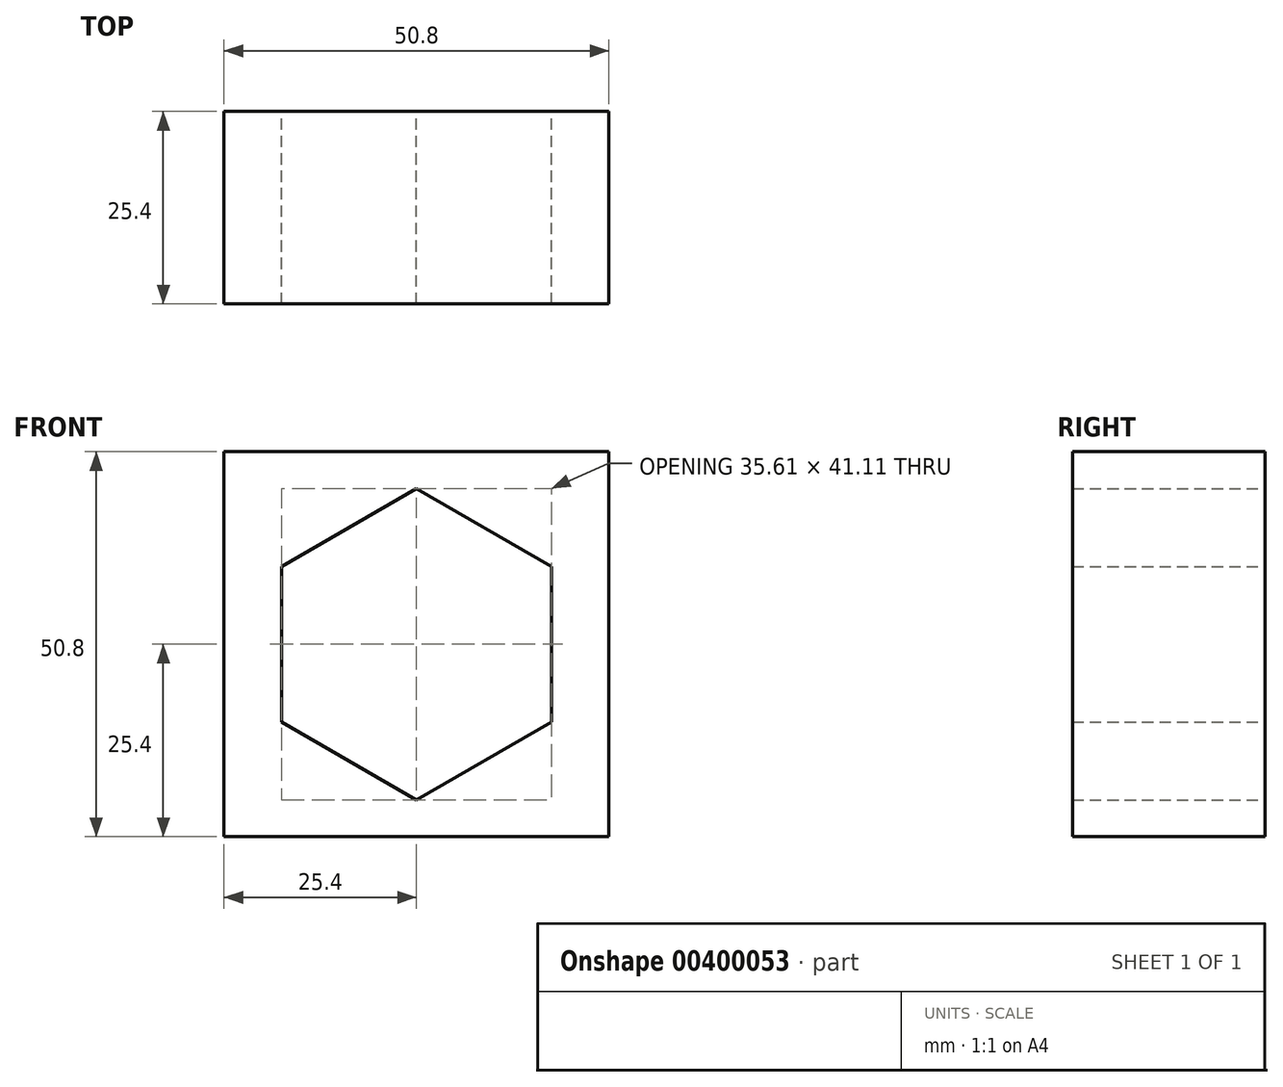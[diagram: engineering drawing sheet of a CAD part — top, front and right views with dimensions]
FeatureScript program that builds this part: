
annotation { "Feature Type Name" : "Feature", "Feature Type Description" : "" }
export const myFeature = defineFeature(function(context is Context, id is Id, definition is map)
    precondition{}
    {
        {
            var Q0;
            Q0=qCreatedBy(makeId("Front.planeOp"),FACE);
            var sketch = newSketch(context, id + "F0", { "sketchPlane" : qUnion([Q0])});
            skLineSegment(sketch, "E0.bottom", {"start": v(0, 0) * mm, "end": v(50.8, 0) * mm});
            skLineSegment(sketch, "E0.top", {"start": v(0, 50.8) * mm, "end": v(50.8, 50.8) * mm});
            skLineSegment(sketch, "E0.left", {"start": v(0, 0) * mm, "end": v(0, 50.8) * mm});
            skLineSegment(sketch, "E0.right", {"start": v(50.8, 0) * mm, "end": v(50.8, 50.8) * mm});
            skCircle(sketch, "E1.cCircle", {"center": v(25.4, 25.4) * mm, "radius": 17.8 * mm, "construction": true});
            skLineSegment(sketch, "E1.0", {"start": v(43.2, 35.68) * mm, "end": v(43.2, 15.12) * mm});
            skLineSegment(sketch, "E1.1", {"start": v(43.2, 15.12) * mm, "end": v(25.4, 4.84) * mm});
            skLineSegment(sketch, "E1.2", {"start": v(25.4, 4.84) * mm, "end": v(7.6, 15.12) * mm});
            skLineSegment(sketch, "E1.3", {"start": v(7.6, 15.12) * mm, "end": v(7.6, 35.68) * mm});
            skLineSegment(sketch, "E1.4", {"start": v(7.6, 35.68) * mm, "end": v(25.4, 45.96) * mm});
            skLineSegment(sketch, "E1.5", {"start": v(25.4, 45.96) * mm, "end": v(43.2, 35.68) * mm});
            skPoint(sketch, "E1.0.midPoint", {"position": v(43.2, 25.4) * mm});
            skSolve(sketch);
        }
        {
            var Q0;
            Q0=makeQuery(id+"F0.imprint","IMPRINT",FACE,{"disambiguationData":[TD([[makeQuery(id+"F0.imprint","IMPRINT",EDGE,{"derivedFrom":sQuery(id+"F0.wireOp",EDGE,"E0.bottom")}),1.0]])]});
            extrude(context, id + "F1", {"entities" : qUnion([Q0]), "depth" : 25.4 * mm});
        }
    });
